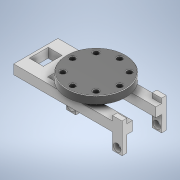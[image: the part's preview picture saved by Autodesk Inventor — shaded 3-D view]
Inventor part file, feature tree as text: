
AUTODESK INVENTOR PART (.ipt)
format: ipt  version: 2021 (Build 250183000, 183)  size: 320,512 bytes
history: native  units: mm
features: sketch x23, extrude x12, fillet x1
ambient origin geometry x8: Origin, YZ Plane, XZ Plane, XY Plane, X Axis, Y Axis, Z Axis, Center Point
bodies: Solid1 (feature_tree)
feature tree (36):
  extrude  "Extrusion1"  Depth=25.0mm
  fillet  "Fillet1"  Radius=25.0mm
  extrude  "Extrusion5"  Depth=8.0mm TaperAngle=0.0deg
  sketch  "Sketch9"  dims[d10=0.5mm d27=12.5mm]
  sketch  "Sketch10"  dims[d28=21.0mm d29=10.0mm]
  sketch  "Sketch11"  dims[d30=5.0mm d31=12.5mm]
  sketch  "Sketch12"  dims[d32=21.0mm d33=10.0mm]
  extrude  "Extrusion7"  Depth=0.5mm
  sketch  "Sketch14"  dims[d37=50.0mm d38=5.0mm]
  extrude  "Extrusion8"  Depth=10.0mm
  extrude  "Extrusion9"  Depth=5.0mm
  sketch  "Sketch19"  dims[d41=5.0mm d42=6.0mm]
  sketch  "Sketch20"  dims[d43=5.0mm d44=6.0mm]
  sketch  "Sketch21"  dims[d45=10.0mm d46=5.0mm]
  extrude  "Extrusion10"  Depth=10.0mm
  extrude  "Extrusion11"  Depth=25.0mm TaperAngle=0.0deg
  sketch  "Sketch24"  dims[d51=40.0mm d52=0.0mm]
  sketch  "Sketch25"  dims[d53=32.0mm d54=0.0mm]
  sketch  "Sketch26"  dims[d55=5.0mm]
  extrude  "Extrusion12"  Depth=5.0mm
  extrude  "Extrusion13"  Depth=50.0mm
  extrude  "Extrusion14"  Depth=6.0mm
  sketch  "Sketch30"  dims[d60=10.0mm]
  extrude  "Extrusion15"  Depth=6.0mm
  extrude  "Extrusion16"  Depth=5.0mm
  sketch  "Sketch1"  dims[d0=62.5mm d2=5.5mm d3=25.0mm]
  sketch  "Sketch8"  dims[d4=80.0mm d6=360.0deg d8=8.0mm d9=0.0mm]
  sketch  "Sketch13"  dims[d34=5.0mm d35=25.0mm d36=0.0mm]
  sketch  "Sketch18"  dims[d39=10.0mm d40=50.0mm]
  sketch  "Sketch22"  dims[d49=5.0mm]
  sketch  "Sketch23"  dims[d50=8.0mm]
  sketch  "Sketch27"  dims[d56=8.0mm]
  sketch  "Sketch28"  dims[d57=60.0mm d58=0.0mm]
  sketch  "Sketch29"  dims[d59=5.0mm]
  sketch  "Sketch31"  dims[d61=65.0mm d62=0.0mm]
  sketch  "Sketch32"  dims[d63=5.0mm d64=10.0mm d65=65.0mm d66=0.0mm d67=55.0mm d68=0.0mm d69=55.0mm d70=0.0mm d71=35.0mm d72=10.0mm d73=0.0mm d74=5.0mm d75=35.0mm d76=0.0mm d77=27.0mm d78=10.0mm d79=15.0mm d80=20.0mm d81=35.0mm d82=0.0mm d16=0.5mm d17=0.872665mm d18=0.5mm d19=0.872665mm d21=0.5mm d22=0.872665mm d23=0.5mm d24=0.872665mm]
